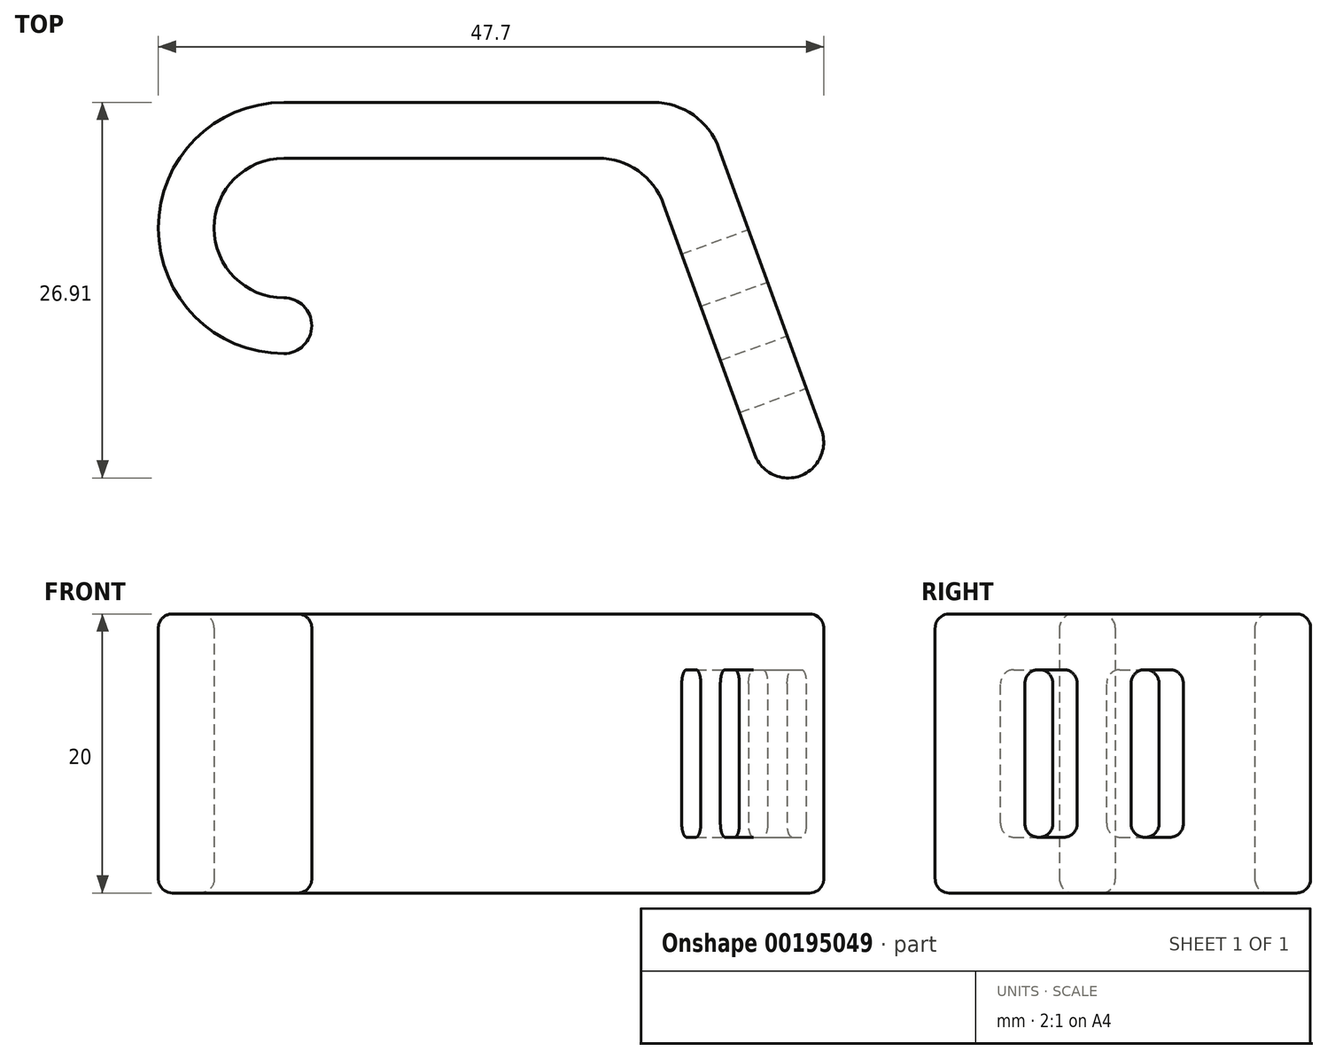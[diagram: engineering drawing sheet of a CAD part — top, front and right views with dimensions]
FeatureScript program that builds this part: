
annotation { "Feature Type Name" : "Feature", "Feature Type Description" : "" }
export const myFeature = defineFeature(function(context is Context, id is Id, definition is map)
    precondition{}
    {
        {
            var Q0;
            Q0=qCreatedBy(makeId("Top.planeOp"),FACE);
            var sketch = newSketch(context, id + "F0", { "sketchPlane" : qUnion([Q0])});
            skLineSegment(sketch, "E0", {"start": v(0, 0) * mm, "end": v(30, 0) * mm});
            skLineSegment(sketch, "E1", {"start": v(30, 0) * mm, "end": v(38.55, -23.5) * mm});
            skArc(sketch, "E2", {"start": v(0, 0) * mm, "mid": v(-9, -9) * mm, "end": v(0, -18) * mm});
            skLineSegment(sketch, "E3", {"start": v(0, -4) * mm, "end": v(26.03, -4) * mm});
            skArc(sketch, "E4", {"start": v(0, -14) * mm, "mid": v(2, -16) * mm, "end": v(0, -18) * mm});
            skArc(sketch, "E5", {"start": v(0, -4) * mm, "mid": v(-5, -9) * mm, "end": v(0, -14) * mm});
            skLineSegment(sketch, "E6", {"start": v(38.55, -23.5) * mm, "end": v(33.76, -25.24) * mm, "construction": true});
            skLineSegment(sketch, "E7", {"start": v(26.03, -4) * mm, "end": v(33.76, -25.24) * mm});
            skLineSegment(sketch, "E8", {"start": v(26.03, -4) * mm, "end": v(26.03, 0) * mm, "construction": true});
            skArc(sketch, "E9", {"start": v(33.76, -25.24) * mm, "mid": v(37.03, -26.76) * mm, "end": v(38.55, -23.5) * mm});
            skSolve(sketch);
        }
        {
            var Q0;
            Q0=makeQuery(id+"F0.imprint","IMPRINT",FACE,{"disambiguationData":[TD([[makeQuery(id+"F0.imprint","IMPRINT",EDGE,{"derivedFrom":sQuery(id+"F0.wireOp",EDGE,"E0")}),-1.0]])]});
            extrude(context, id + "F1", {"entities" : qUnion([Q0]), "depth" : 20 * mm});
        }
        {
            var Q0;
            Q0=makeQuery(id+"F1.opExtrude","SWEPT_FACE",FACE,{"disambiguationData":[OSD([sQuery(id+"F0.wireOp",EDGE,"E1")])]});
            var sketch = newSketch(context, id + "F2", { "sketchPlane" : qUnion([Q0])});
            skLineSegment(sketch, "E10.bottom", {"start": v(-29.06, 16) * mm, "end": v(-31.06, 16) * mm});
            skLineSegment(sketch, "E10.top", {"start": v(-29.06, 4) * mm, "end": v(-31.06, 4) * mm});
            skLineSegment(sketch, "E10.left", {"start": v(-28.06, 15) * mm, "end": v(-28.06, 5) * mm});
            skLineSegment(sketch, "E10.right", {"start": v(-32.06, 15) * mm, "end": v(-32.06, 5) * mm});
            skLineSegment(sketch, "E11", {"start": v(-35.26, 20) * mm, "end": v(-35.26, 0) * mm, "construction": true});
            skPoint(sketch, "E12", {"position": v(-35.26, 10) * mm});
            skPoint(sketch, "E13", {"position": v(-32.06, 10) * mm});
            skLineSegment(sketch, "E14", {"start": v(-35.26, 10) * mm, "end": v(-32.06, 10) * mm, "construction": true});
            skLineSegment(sketch, "E15", {"start": v(-28.06, 10) * mm, "end": v(-23.96, 10) * mm, "construction": true});
            skLineSegment(sketch, "E16.bottom", {"start": v(-20.96, 16) * mm, "end": v(-22.96, 16) * mm});
            skLineSegment(sketch, "E16.top", {"start": v(-20.96, 4) * mm, "end": v(-22.96, 4) * mm});
            skLineSegment(sketch, "E16.left", {"start": v(-19.96, 15) * mm, "end": v(-19.96, 5) * mm});
            skLineSegment(sketch, "E16.right", {"start": v(-23.96, 15) * mm, "end": v(-23.96, 5) * mm});
            skPoint(sketch, "E17", {"position": v(-23.96, 10) * mm});
            skPoint(sketch, "E18.visualSharp", {"position": v(-19.96, 4) * mm});
            skArc(sketch, "E18.filletArc", {"start": v(-20.96, 4) * mm, "mid": v(-20.25, 4.3) * mm, "end": v(-19.96, 5) * mm});
            skPoint(sketch, "E19.visualSharp", {"position": v(-23.96, 16) * mm});
            skArc(sketch, "E19.filletArc", {"start": v(-22.96, 16) * mm, "mid": v(-23.67, 15.7) * mm, "end": v(-23.96, 15) * mm});
            skPoint(sketch, "E20.visualSharp", {"position": v(-23.96, 4) * mm});
            skArc(sketch, "E20.filletArc", {"start": v(-23.96, 5) * mm, "mid": v(-23.67, 4.3) * mm, "end": v(-22.96, 4) * mm});
            skPoint(sketch, "E21.visualSharp", {"position": v(-19.96, 16) * mm});
            skArc(sketch, "E21.filletArc", {"start": v(-19.96, 15) * mm, "mid": v(-20.25, 15.7) * mm, "end": v(-20.96, 16) * mm});
            skPoint(sketch, "E22.visualSharp", {"position": v(-28.06, 4) * mm});
            skArc(sketch, "E22.filletArc", {"start": v(-29.06, 4) * mm, "mid": v(-28.35, 4.3) * mm, "end": v(-28.06, 5) * mm});
            skPoint(sketch, "E23.visualSharp", {"position": v(-32.06, 4) * mm});
            skArc(sketch, "E23.filletArc", {"start": v(-32.06, 5) * mm, "mid": v(-31.77, 4.3) * mm, "end": v(-31.06, 4) * mm});
            skPoint(sketch, "E24.visualSharp", {"position": v(-28.06, 16) * mm});
            skArc(sketch, "E24.filletArc", {"start": v(-28.06, 15) * mm, "mid": v(-28.35, 15.7) * mm, "end": v(-29.06, 16) * mm});
            skPoint(sketch, "E25.visualSharp", {"position": v(-32.06, 16) * mm});
            skArc(sketch, "E25.filletArc", {"start": v(-31.06, 16) * mm, "mid": v(-31.77, 15.7) * mm, "end": v(-32.06, 15) * mm});
            skSolve(sketch);
        }
        {
            var Q0;
            Q0=makeQuery(id+"F2.imprint","IMPRINT",FACE,{"disambiguationData":[TD([[makeQuery(id+"F2.imprint","IMPRINT",EDGE,{"derivedFrom":sQuery(id+"F2.wireOp",EDGE,"E16.bottom")}),1.0]])]});
            var Q1;
            Q1=makeQuery(id+"F2.imprint","IMPRINT",FACE,{"disambiguationData":[TD([[makeQuery(id+"F2.imprint","IMPRINT",EDGE,{"derivedFrom":sQuery(id+"F2.wireOp",EDGE,"E10.bottom")}),1.0]])]});
            var Q2;
            Q2=makeQuery(id+"F1.opExtrude","SWEPT_FACE",FACE,{"disambiguationData":[OSD([sQuery(id+"F0.wireOp",EDGE,"E7")])]});
            extrude(context, id + "F3", {"entities" : qUnion([Q0, Q1]), "operationType" : NewBodyOperationType.REMOVE, "endBound" : BoundingType.UP_TO_SURFACE, "oppositeDirection" : true, "endBoundEntityFace" : qUnion([Q2]), "depth" : 25 * mm});
        }
        {
            var Q0;
            Q0=makeQuery(id+"F1.opExtrude","SWEPT_EDGE",EDGE,{"disambiguationData":[OSD([sQuery(id+"F0.wireOp",EDGE,"E3"),sQuery(id+"F0.wireOp",EDGE,"E7")])]});
            fillet(context, id + "F4", {"entities" : qUnion([Q0]), "radius" : 5 * mm, "tangentPropagation" : true, "allowEdgeOverflow" : false});
        }
        {
            var Q0;
            Q0=makeQuery(id+"F1.opExtrude","CAP_EDGE",EDGE,{"disambiguationData":[OSD([sQuery(id+"F0.wireOp",EDGE,"E0")])],"isStart":false});
            var Q1;
            Q1=makeQuery(id+"F1.opExtrude","CAP_FACE",FACE,{"disambiguationData":[OSD([sQuery(id+"F0.wireOp",EDGE,"E0"),sQuery(id+"F0.wireOp",EDGE,"E1"),sQuery(id+"F0.wireOp",EDGE,"E2"),sQuery(id+"F0.wireOp",EDGE,"E3"),sQuery(id+"F0.wireOp",EDGE,"E4"),sQuery(id+"F0.wireOp",EDGE,"E5"),sQuery(id+"F0.wireOp",EDGE,"E7"),sQuery(id+"F0.wireOp",EDGE,"E9")])],"isStart":false});
            fillet(context, id + "F5", {"entities" : qUnion([Q0, Q1]), "radius" : 1 * mm, "tangentPropagation" : true, "allowEdgeOverflow" : false});
        }
        {
            var Q0;
            Q0=makeQuery(id+"F1.opExtrude","CAP_FACE",FACE,{"disambiguationData":[OSD([sQuery(id+"F0.wireOp",EDGE,"E0"),sQuery(id+"F0.wireOp",EDGE,"E1"),sQuery(id+"F0.wireOp",EDGE,"E2"),sQuery(id+"F0.wireOp",EDGE,"E3"),sQuery(id+"F0.wireOp",EDGE,"E4"),sQuery(id+"F0.wireOp",EDGE,"E5"),sQuery(id+"F0.wireOp",EDGE,"E7"),sQuery(id+"F0.wireOp",EDGE,"E9")])],"isStart":true});
            fillet(context, id + "F6", {"entities" : qUnion([Q0]), "radius" : 1 * mm, "tangentPropagation" : true, "allowEdgeOverflow" : false});
        }
        {
            var Q0;
            Q0=makeQuery(id+"F1.opExtrude","SWEPT_EDGE",EDGE,{"disambiguationData":[OSD([sQuery(id+"F0.wireOp",EDGE,"E0"),sQuery(id+"F0.wireOp",EDGE,"E1")])]});
            fillet(context, id + "F7", {"entities" : qUnion([Q0]), "radius" : 5 * mm, "tangentPropagation" : true, "allowEdgeOverflow" : false});
        }
    });
